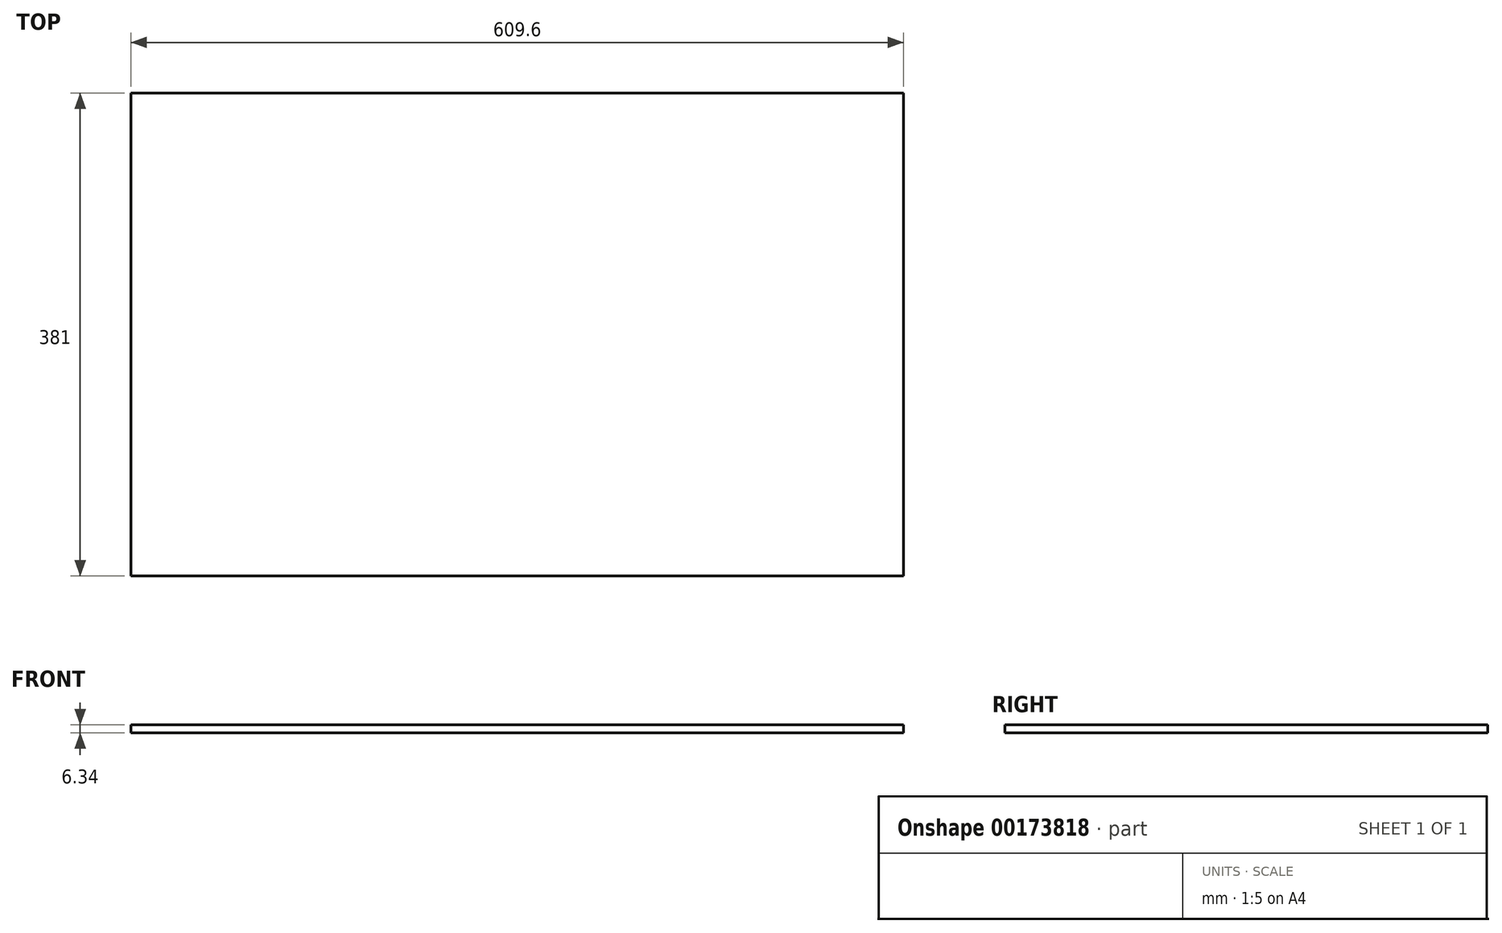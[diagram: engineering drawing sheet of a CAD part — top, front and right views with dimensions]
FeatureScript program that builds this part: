
annotation { "Feature Type Name" : "Feature", "Feature Type Description" : "" }
export const myFeature = defineFeature(function(context is Context, id is Id, definition is map)
    precondition{}
    {
        {
            var Q0;
            Q0=qCreatedBy(makeId("Top.planeOp"),FACE);
            var sketch = newSketch(context, id + "F0", { "sketchPlane" : qUnion([Q0])});
            skLineSegment(sketch, "E0.bottom", {"start": v(-315.3, 351.56) * mm, "end": v(294.3, 351.56) * mm});
            skLineSegment(sketch, "E0.top", {"start": v(-315.3, -29.44) * mm, "end": v(294.3, -29.44) * mm});
            skLineSegment(sketch, "E0.left", {"start": v(-315.3, 351.56) * mm, "end": v(-315.3, -29.44) * mm});
            skLineSegment(sketch, "E0.right", {"start": v(294.3, 351.56) * mm, "end": v(294.3, -29.44) * mm});
            skSolve(sketch);
        }
        {
            var Q0;
            Q0 = qSketchRegion(id + "F0", true);
            extrude(context, id + "F1", {"entities" : qUnion([Q0]), "endBound" : BoundingType.SYMMETRIC, "depth" : 6.35 * mm});
        }
    });
